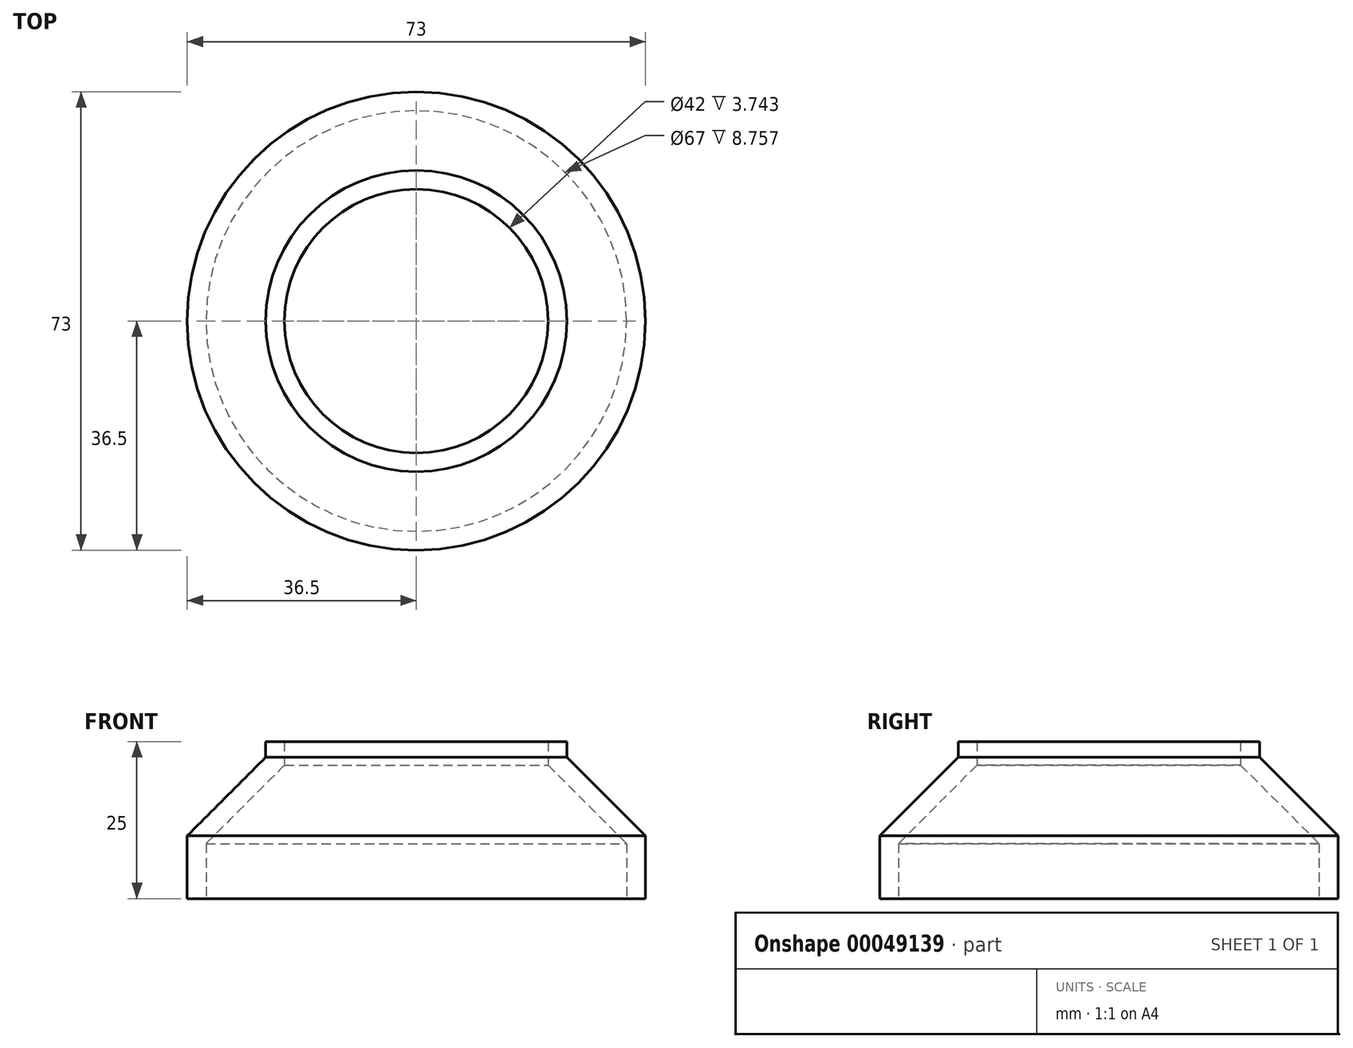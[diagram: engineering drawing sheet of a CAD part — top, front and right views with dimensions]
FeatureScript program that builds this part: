
annotation { "Feature Type Name" : "Feature", "Feature Type Description" : "" }
export const myFeature = defineFeature(function(context is Context, id is Id, definition is map)
    precondition{}
    {
        {
            var Q0;
            Q0=qCreatedBy(makeId("Front.planeOp"),FACE);
            var sketch = newSketch(context, id + "F0", { "sketchPlane" : qUnion([Q0])});
            skLineSegment(sketch, "E0", {"start": v(36.5, 0) * mm, "end": v(36.5, 10) * mm});
            skLineSegment(sketch, "E1", {"start": v(36.5, 10) * mm, "end": v(24, 22.5) * mm});
            skLineSegment(sketch, "E2", {"start": v(24, 22.5) * mm, "end": v(24, 25) * mm});
            skLineSegment(sketch, "E3.0", {"start": v(21, 21.26) * mm, "end": v(21, 25) * mm});
            skLineSegment(sketch, "E3.1", {"start": v(33.5, 8.76) * mm, "end": v(21, 21.26) * mm});
            skLineSegment(sketch, "E3.2", {"start": v(33.5, 0) * mm, "end": v(33.5, 8.76) * mm});
            skLineSegment(sketch, "E4", {"start": v(24, 25) * mm, "end": v(21, 25) * mm});
            skLineSegment(sketch, "E5", {"start": v(33.5, 0) * mm, "end": v(36.5, 0) * mm});
            skLineSegment(sketch, "E6", {"start": v(0, 0) * mm, "end": v(0, 82.27) * mm});
            skSolve(sketch);
        }
        {
            var Q0;
            Q0=makeQuery(id+"F0.imprint","IMPRINT",FACE,{"disambiguationData":[TD([[makeQuery(id+"F0.imprint","IMPRINT",EDGE,{"derivedFrom":sQuery(id+"F0.wireOp",EDGE,"E0")}),1.0]])]});
            var Q1;
            Q1=sQuery(id+"F0.wireOp",EDGE,"E6");
            revolve(context, id + "F1", {"entities" : qUnion([Q0]), "axis" : qUnion([Q1]), "revolveType" : RevolveType.FULL});
        }
    });
